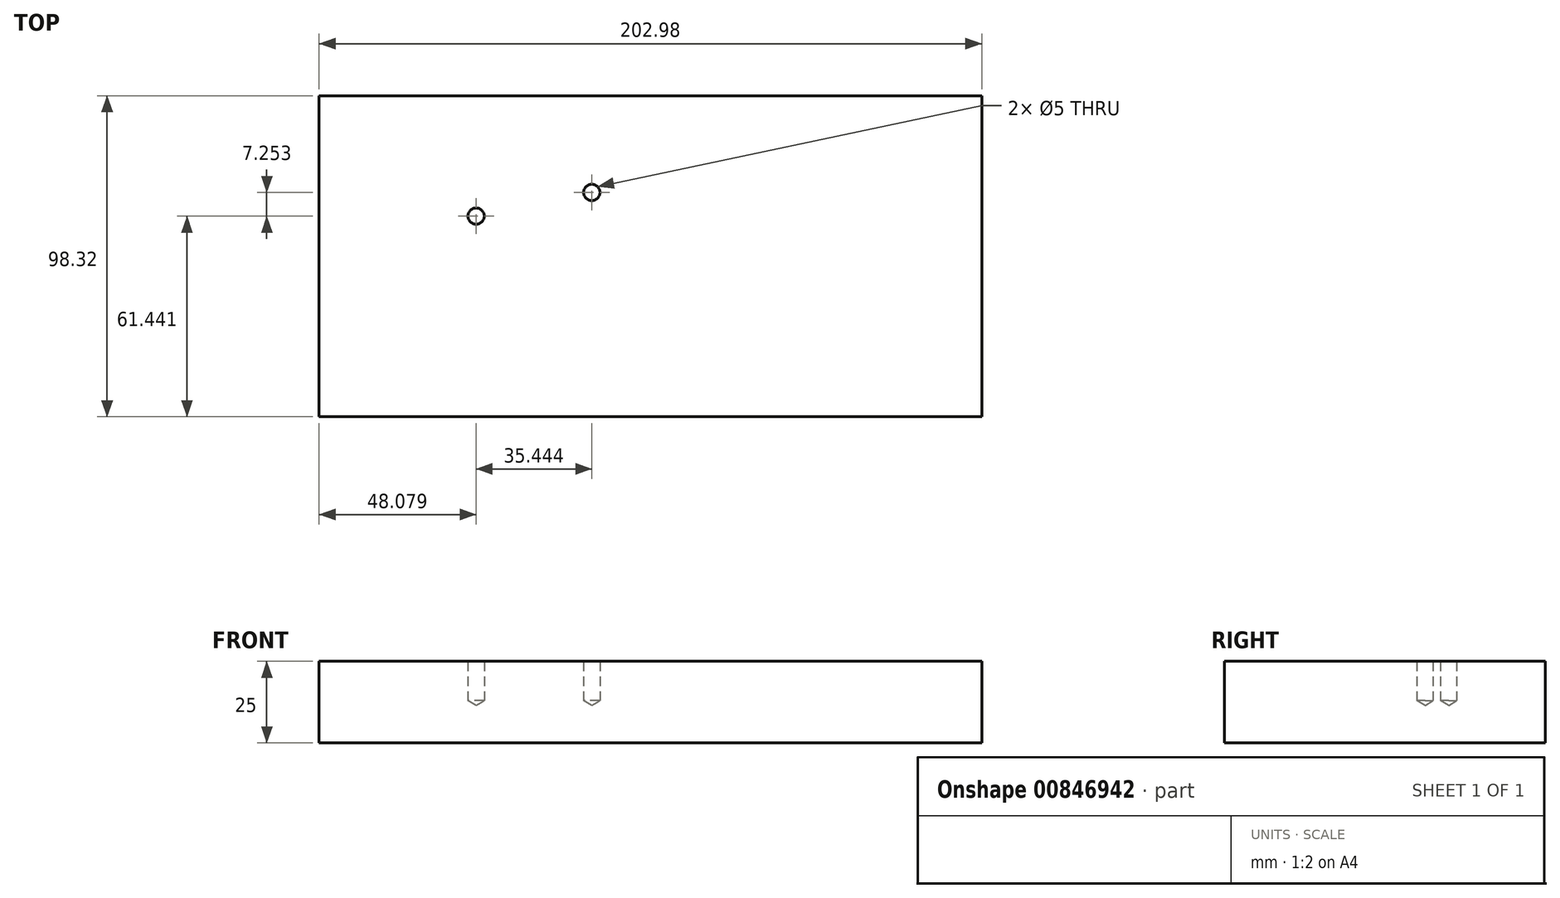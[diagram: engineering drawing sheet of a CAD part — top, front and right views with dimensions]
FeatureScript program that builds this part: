
annotation { "Feature Type Name" : "Feature", "Feature Type Description" : "" }
export const myFeature = defineFeature(function(context is Context, id is Id, definition is map)
    precondition{}
    {
        {
            var Q0;
            Q0=qCreatedBy(makeId("Top.planeOp"),FACE);
            var sketch = newSketch(context, id + "F0", { "sketchPlane" : qUnion([Q0])});
            skLineSegment(sketch, "E0.bottom", {"start": v(-101.5, -45.94) * mm, "end": v(11.84, -45.94) * mm});
            skLineSegment(sketch, "E0.top", {"start": v(-101.5, -144.26) * mm, "end": v(11.84, -144.26) * mm});
            skLineSegment(sketch, "E0.left", {"start": v(-101.5, -45.94) * mm, "end": v(-101.5, -144.26) * mm});
            skLineSegment(sketch, "E0.right", {"start": v(11.84, -45.94) * mm, "end": v(11.84, -144.26) * mm});
            skSolve(sketch);
        }
        {
            var Q0;
            Q0=qSketchRegion(id+"F0",true);
            extrude(context, id + "F1", {"entities" : qUnion([Q0]), "depth" : 25 * mm, "offsetDistance" : 25 * mm});
        }
        {
            var Q0;
            Q0=makeQuery(id+"F1.opExtrude","SWEPT_BODY",BODY,{"disambiguationData":[OSD([sQuery(id+"F0.wireOp",EDGE,"E0.bottom"),sQuery(id+"F0.wireOp",EDGE,"E0.top"),sQuery(id+"F0.wireOp",EDGE,"E0.left"),sQuery(id+"F0.wireOp",EDGE,"E0.right")])]});
            var Q1;
            Q1=qCreatedBy(makeId("Right.planeOp"),FACE);
            mirror(context, id + "F2", {"operationType" : NewBodyOperationType.ADD, "entities" : qUnion([Q0]), "mirrorPlane" : qUnion([Q1])});
        }
        {
            var Q0;
            {var subQ0=makeQuery(id+"F1.opExtrude","CAP_FACE",FACE,{"disambiguationData":[OSD([sQuery(id+"F0.wireOp",EDGE,"E0.bottom"),sQuery(id+"F0.wireOp",EDGE,"E0.top"),sQuery(id+"F0.wireOp",EDGE,"E0.left"),sQuery(id+"F0.wireOp",EDGE,"E0.right")])],"isStart":false});Q0=makeQuery(id+"F2.boolean.opBoolean","MERGE",FACE,{"derivedFrom":[subQ0,makeQuery(id+"F2.opPattern","COPY",FACE,{"derivedFrom":subQ0,"instanceName":"1"})]});}
            var sketch = newSketch(context, id + "F3", { "sketchPlane" : qUnion([Q0])});
            skPoint(sketch, "E1", {"position": v(-53.41, -82.82) * mm});
            skPoint(sketch, "E2", {"position": v(-17.97, -75.57) * mm});
            skPoint(sketch, "E3", {"position": v(42.5, -79.62) * mm});
            skSolve(sketch);
        }
        {
            var Q0;
            Q0=sQuery(id+"F3.wireOp",VERTEX,"E1");
            var Q1;
            Q1=sQuery(id+"F3.wireOp",VERTEX,"E2");
            var Q2;
            Q2=makeQuery(id+"F1.opExtrude","SWEPT_BODY",BODY,{"disambiguationData":[OSD([sQuery(id+"F0.wireOp",EDGE,"E0.bottom"),sQuery(id+"F0.wireOp",EDGE,"E0.top"),sQuery(id+"F0.wireOp",EDGE,"E0.left"),sQuery(id+"F0.wireOp",EDGE,"E0.right")])]});
            hole(context, id + "F4", {"style" : HoleStyle.SIMPLE, "endStyle" : HoleEndStyle.BLIND, "holeDiameter" : 5 * mm, "majorDiameter" : 5 * mm, "holeDepth" : 12 * mm, "isTappedThrough" : true, "tappedDepth" : 12 * mm, "tapClearance" : 3, "locations" : qUnion([Q0, Q1]), "scope" : qUnion([Q2]), "startStyle" : HoleStartStyle.PART});
        }
    });
